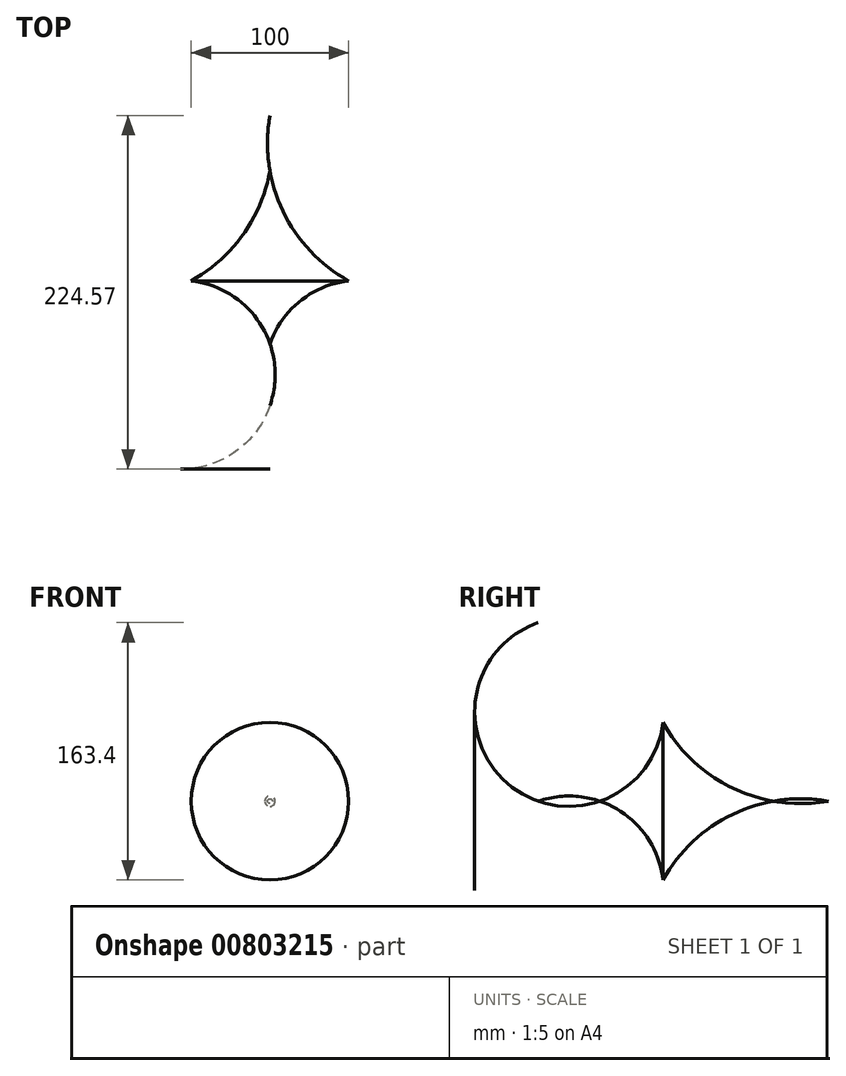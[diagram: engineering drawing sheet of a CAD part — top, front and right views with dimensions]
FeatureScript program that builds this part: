
annotation { "Feature Type Name" : "Feature", "Feature Type Description" : "" }
export const myFeature = defineFeature(function(context is Context, id is Id, definition is map)
    precondition{}
    {
        {
            var Q0;
            Q0=qCreatedBy(makeId("Top.planeOp"),FACE);
            var sketch = newSketch(context, id + "F0", { "sketchPlane" : qUnion([Q0])});
            skLineSegment(sketch, "E0", {"start": v(0, 0) * mm, "end": v(0, 77.9) * mm, "construction": true});
            skLineSegment(sketch, "E1", {"start": v(0, 0) * mm, "end": v(0, -76.6) * mm, "construction": true});
            skArc(sketch, "E2", {"start": v(50, 0) * mm, "mid": v(19.22, -12.77) * mm, "end": v(0, -40) * mm});
            skArc(sketch, "E3", {"start": v(0, 70) * mm, "mid": v(17.09, 29.35) * mm, "end": v(50, 0) * mm});
            skLineSegment(sketch, "E4", {"start": v(0, 70) * mm, "end": v(0, -40) * mm});
            skSolve(sketch);
        }
        {
            var Q0;
            Q0=makeQuery(id+"F0.imprint","IMPRINT",FACE,{"disambiguationData":[TD([[makeQuery(id+"F0.imprint","IMPRINT",EDGE,{"derivedFrom":sQuery(id+"F0.wireOp",EDGE,"E2")}),-1.0]])]});
            var Q1;
            Q1=sQuery(id+"F0.wireOp",EDGE,"E1");
            revolve(context, id + "F1", {"surfaceOperationType" : NewSurfaceOperationType.NEW, "entities" : qUnion([Q0]), "axis" : qUnion([Q1]), "revolveType" : RevolveType.FULL});
        }
    });
